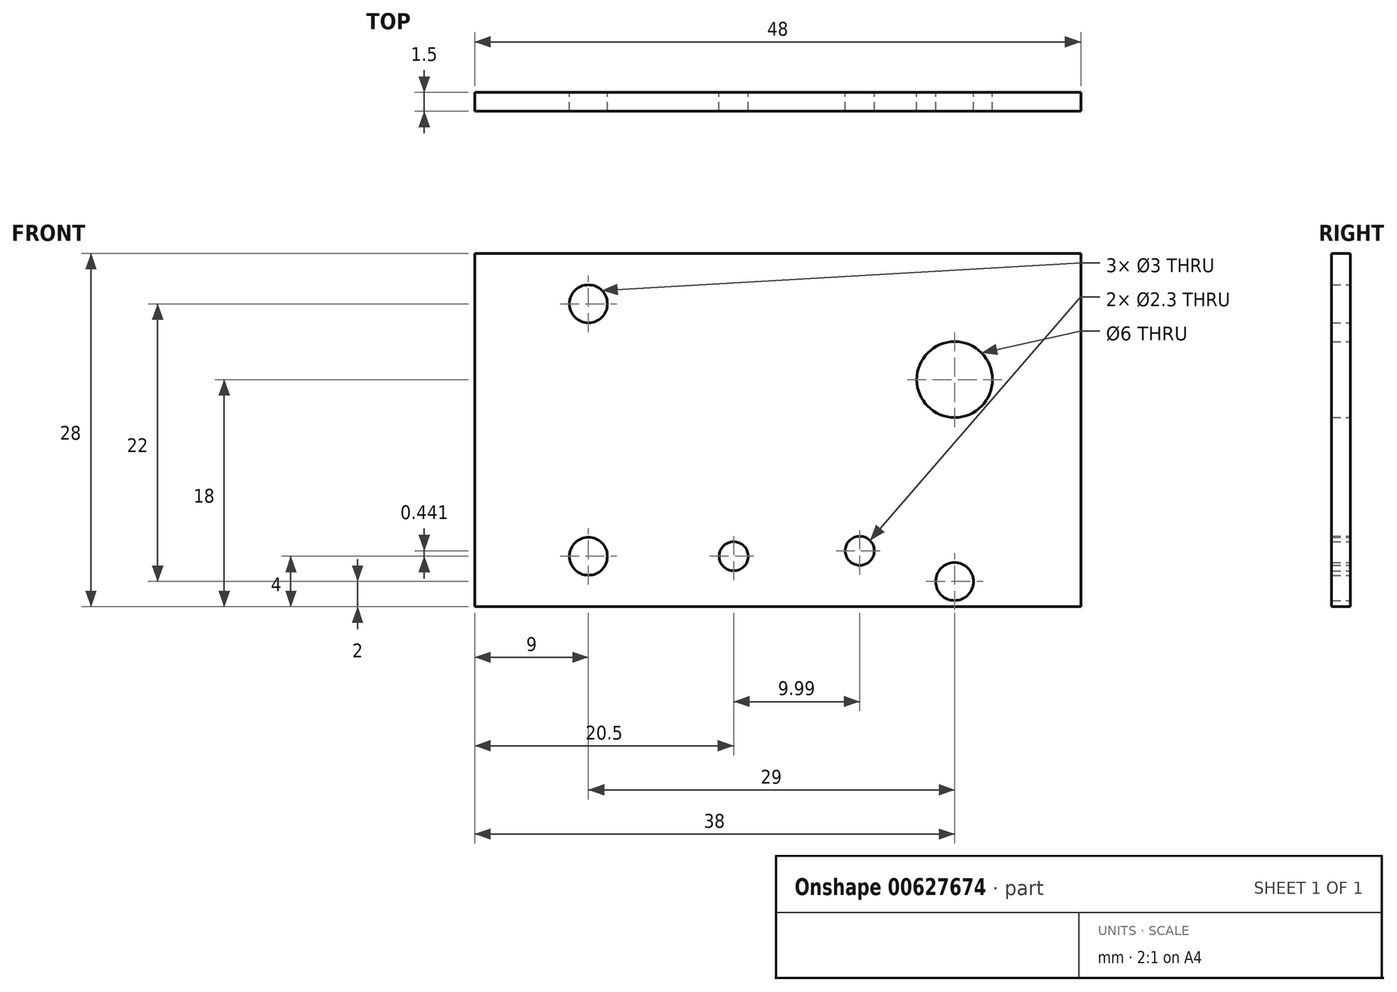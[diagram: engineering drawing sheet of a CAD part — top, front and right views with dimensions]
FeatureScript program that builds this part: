
annotation { "Feature Type Name" : "Feature", "Feature Type Description" : "" }
export const myFeature = defineFeature(function(context is Context, id is Id, definition is map)
    precondition{}
    {
        {
            var Q0;
            Q0=qCreatedBy(makeId("Front.planeOp"),FACE);
            var sketch = newSketch(context, id + "F0", { "sketchPlane" : qUnion([Q0])});
            skLineSegment(sketch, "E0.bottom", {"start": v(0, 0) * mm, "end": v(40, 0) * mm});
            skLineSegment(sketch, "E0.top", {"start": v(0, -28) * mm, "end": v(40, -28) * mm});
            skLineSegment(sketch, "E0.left", {"start": v(0, 0) * mm, "end": v(0, -28) * mm});
            skLineSegment(sketch, "E0.right", {"start": v(40, 0) * mm, "end": v(40, -28) * mm});
            skSolve(sketch);
        }
        {
            var Q0;
            Q0=makeQuery(id+"F0.imprint","IMPRINT",FACE,{"disambiguationData":[TD([[makeQuery(id+"F0.imprint","IMPRINT",EDGE,{"derivedFrom":sQuery(id+"F0.wireOp",EDGE,"E0.bottom")}),-1.0]])]});
            extrude(context, id + "F1", {"entities" : qUnion([Q0]), "depth" : 1.5 * mm, "offsetDistance" : 25 * mm});
        }
        {
            var Q0;
            Q0=makeQuery(id+"F1.opExtrude","CAP_FACE",FACE,{"disambiguationData":[OSD([sQuery(id+"F0.wireOp",EDGE,"E0.bottom"),sQuery(id+"F0.wireOp",EDGE,"E0.top"),sQuery(id+"F0.wireOp",EDGE,"E0.left"),sQuery(id+"F0.wireOp",EDGE,"E0.right")])],"isStart":true});
            var sketch = newSketch(context, id + "F2", { "sketchPlane" : qUnion([Q0])});
            skCircle(sketch, "E1", {"center": v(-20.5, -24) * mm, "radius": 7.5 * mm, "construction": true});
            skCircle(sketch, "E2", {"center": v(-30.5, -23.56) * mm, "radius": 2.5 * mm, "construction": true});
            skCircle(sketch, "E3", {"center": v(-30.5, -23.56) * mm, "radius": 5 * mm, "construction": true});
            skCircle(sketch, "E4", {"center": v(-38, -10) * mm, "radius": 10.5 * mm, "construction": true});
            skCircle(sketch, "E5", {"center": v(-38, -26) * mm, "radius": 2 * mm, "construction": true});
            skCircle(sketch, "E6", {"center": v(-9, -24) * mm, "radius": 2 * mm, "construction": true});
            skCircle(sketch, "E7", {"center": v(-9, -4) * mm, "radius": 2 * mm, "construction": true});
            skSolve(sketch);
        }
        {
            var Q0;
            Q0=makeQuery(id+"F2.imprint","IMPRINT",FACE,{"disambiguationData":[TD([[makeQuery(id+"F2.imprint","IMPRINT",EDGE,{"derivedFrom":makeQuery(id+"F1.opExtrude","CAP_EDGE",EDGE,{"disambiguationData":[OSD([sQuery(id+"F0.wireOp",EDGE,"E0.bottom")])],"isStart":true})}),1.0]])]});
            var sketch = newSketch(context, id + "F3", { "sketchPlane" : qUnion([Q0])});
            skCircle(sketch, "E8.0", {"center": v(-38, -26) * mm, "radius": 1.5 * mm});
            skCircle(sketch, "E9.0", {"center": v(-9, -24) * mm, "radius": 1.5 * mm});
            skCircle(sketch, "E10.0", {"center": v(-9, -4) * mm, "radius": 1.5 * mm});
            skSolve(sketch);
        }
        {
            var Q0;
            Q0 = qSketchRegion(id + "F3", true);
            extrude(context, id + "F4", {"entities" : qUnion([Q0]), "operationType" : NewBodyOperationType.REMOVE, "endBound" : BoundingType.THROUGH_ALL, "oppositeDirection" : true, "depth" : 25 * mm, "offsetDistance" : 25 * mm});
        }
        {
            var Q0;
            Q0=makeQuery(id+"F2.imprint","IMPRINT",FACE,{"disambiguationData":[TD([[makeQuery(id+"F2.imprint","IMPRINT",EDGE,{"derivedFrom":makeQuery(id+"F1.opExtrude","CAP_EDGE",EDGE,{"disambiguationData":[OSD([sQuery(id+"F0.wireOp",EDGE,"E0.bottom")])],"isStart":true})}),1.0]])]});
            var sketch = newSketch(context, id + "F5", { "sketchPlane" : qUnion([Q0])});
            skPoint(sketch, "E11.0", {"position": v(-20.5, -24) * mm});
            skPoint(sketch, "E11.1", {"position": v(-30.5, -23.56) * mm});
            skPoint(sketch, "E11.2", {"position": v(-38, -10) * mm});
            skCircle(sketch, "E12", {"center": v(-20.5, -24) * mm, "radius": 1.15 * mm});
            skCircle(sketch, "E13", {"center": v(-30.5, -23.56) * mm, "radius": 1.15 * mm});
            skSolve(sketch);
        }
        {
            var Q0;
            Q0 = qSketchRegion(id + "F5", true);
            extrude(context, id + "F6", {"entities" : qUnion([Q0]), "operationType" : NewBodyOperationType.REMOVE, "endBound" : BoundingType.THROUGH_ALL, "oppositeDirection" : true, "depth" : 25 * mm, "offsetDistance" : 25 * mm});
        }
        {
            var Q0;
            Q0=makeQuery(id+"F1.opExtrude","SWEPT_FACE",FACE,{"disambiguationData":[OSD([sQuery(id+"F0.wireOp",EDGE,"E0.right")])]});
            var sketch = newSketch(context, id + "F7", { "sketchPlane" : qUnion([Q0])});
            skLineSegment(sketch, "E14.0", {"start": v(0, 0) * mm, "end": v(0, -28) * mm});
            skLineSegment(sketch, "E14.1", {"start": v(-1.5, 0) * mm, "end": v(0, 0) * mm});
            skLineSegment(sketch, "E14.2", {"start": v(-1.5, 0) * mm, "end": v(-1.5, -28) * mm});
            skLineSegment(sketch, "E14.3", {"start": v(-1.5, -28) * mm, "end": v(0, -28) * mm});
            skSolve(sketch);
        }
        {
            var Q0;
            Q0 = qSketchRegion(id + "F7", true);
            extrude(context, id + "F8", {"entities" : qUnion([Q0]), "operationType" : NewBodyOperationType.ADD, "depth" : 8 * mm, "offsetDistance" : 25 * mm});
        }
        {
            var Q0;
            Q0=makeQuery(id+"F8.boolean.opBoolean","MERGE",FACE,{"derivedFrom":[makeQuery(id+"F1.opExtrude","CAP_FACE",FACE,{"disambiguationData":[OSD([sQuery(id+"F0.wireOp",EDGE,"E0.bottom"),sQuery(id+"F0.wireOp",EDGE,"E0.top"),sQuery(id+"F0.wireOp",EDGE,"E0.left"),sQuery(id+"F0.wireOp",EDGE,"E0.right")])],"isStart":true}),makeQuery(id+"F8.opExtrude","SWEPT_FACE",FACE,{"disambiguationData":[OSD([sQuery(id+"F7.wireOp",EDGE,"E14.0")])]})]});
            var sketch = newSketch(context, id + "F9", { "sketchPlane" : qUnion([Q0])});
            skPoint(sketch, "E15.0", {"position": v(-38, -10) * mm});
            skCircle(sketch, "E16", {"center": v(-38, -10) * mm, "radius": 3 * mm});
            skSolve(sketch);
        }
        {
            var Q0;
            Q0 = qSketchRegion(id + "F9", true);
            extrude(context, id + "F10", {"entities" : qUnion([Q0]), "operationType" : NewBodyOperationType.REMOVE, "endBound" : BoundingType.THROUGH_ALL, "oppositeDirection" : true, "depth" : 25 * mm, "offsetDistance" : 25 * mm});
        }
    });
